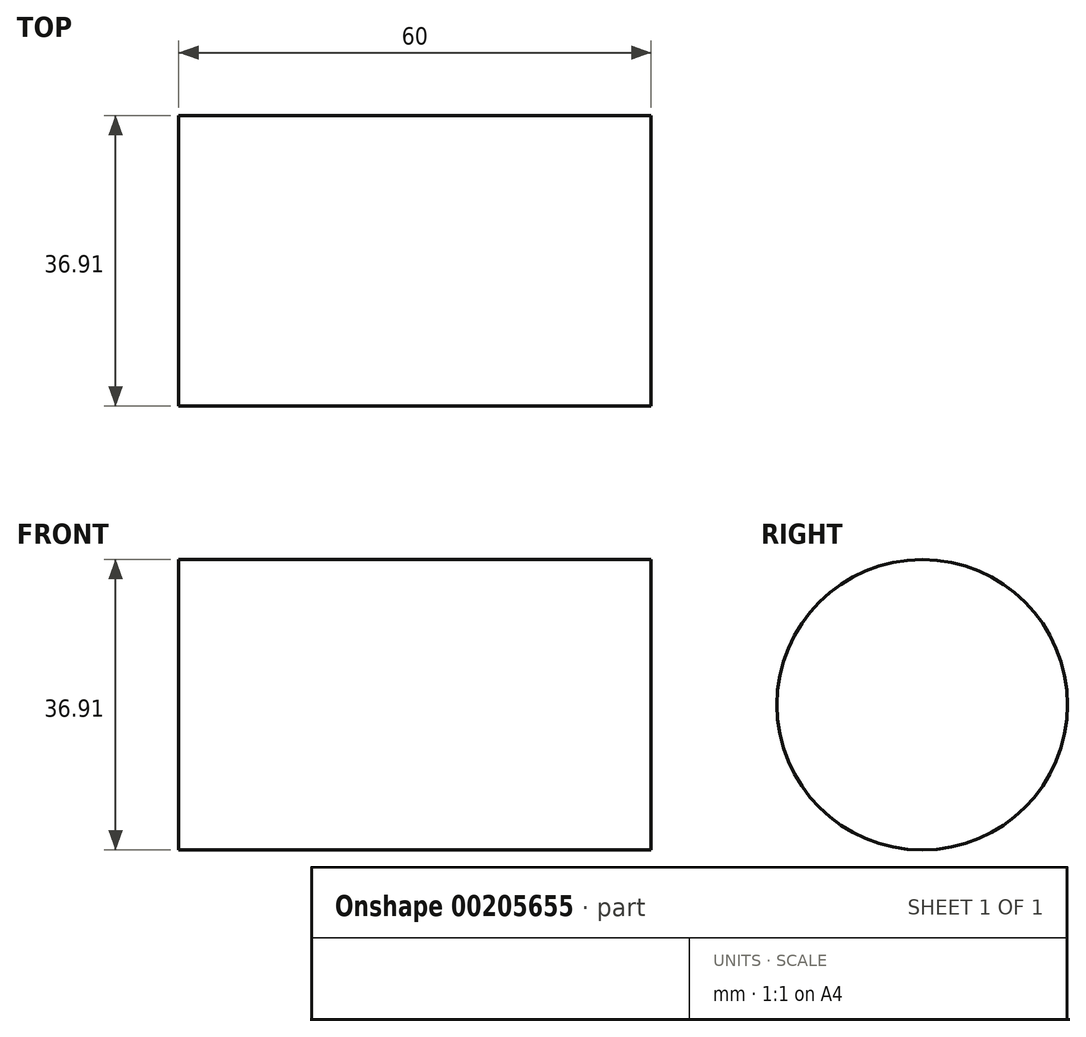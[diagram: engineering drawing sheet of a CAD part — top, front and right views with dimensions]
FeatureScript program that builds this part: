
annotation { "Feature Type Name" : "Feature", "Feature Type Description" : "" }
export const myFeature = defineFeature(function(context is Context, id is Id, definition is map)
    precondition{}
    {
        {
            var Q0;
            Q0=qCreatedBy(makeId("Right.planeOp"),FACE);
            var sketch = newSketch(context, id + "F0", { "sketchPlane" : qUnion([Q0])});
            skCircle(sketch, "E0", {"center": v(-20.8, 21.33) * mm, "radius": 45.4 * mm});
            skCircle(sketch, "E1", {"center": v(25.88, -27.35) * mm, "radius": 19.86 * mm});
            skCircle(sketch, "E2", {"center": v(-55.45, -37.56) * mm, "radius": 18.46 * mm});
            skSolve(sketch);
        }
        {
            var Q0;
            Q0=makeQuery(id+"F0.imprint","IMPRINT",FACE,{"disambiguationData":[TD([[makeQuery(id+"F0.imprint","IMPRINT",EDGE,{"derivedFrom":sQuery(id+"F0.wireOp",EDGE,"E2")}),1.0]])]});
            extrude(context, id + "F1", {"entities" : qUnion([Q0]), "depth" : 60 * mm});
        }
    });
